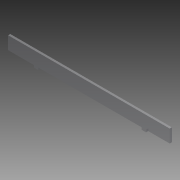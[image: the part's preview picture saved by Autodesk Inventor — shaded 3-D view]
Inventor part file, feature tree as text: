
AUTODESK INVENTOR PART (.ipt)
format: ipt  version: 2013 (Build 170138000, 138)  size: 79,872 bytes
history: native  units: in
note: dims shown in document units (in); Inventor stores cm internally (conversion verified against a paired STEP export)
features: extrude x1, sketch x1
ambient origin geometry x8: Origin, YZ Plane, XZ Plane, XY Plane, X Axis, Y Axis, Z Axis, Center Point
bodies: Solid1 (feature_tree)
feature tree (2):
  extrude  "Extrusion1"  Depth=3.0in
  sketch  "Sketch1"  dims[d0=1.5in d1=3.0in d2=0.25in d3=0.5in d4=12.0in d5=0.5in d6=18.75in d7=0.25in d8=0.0in]
